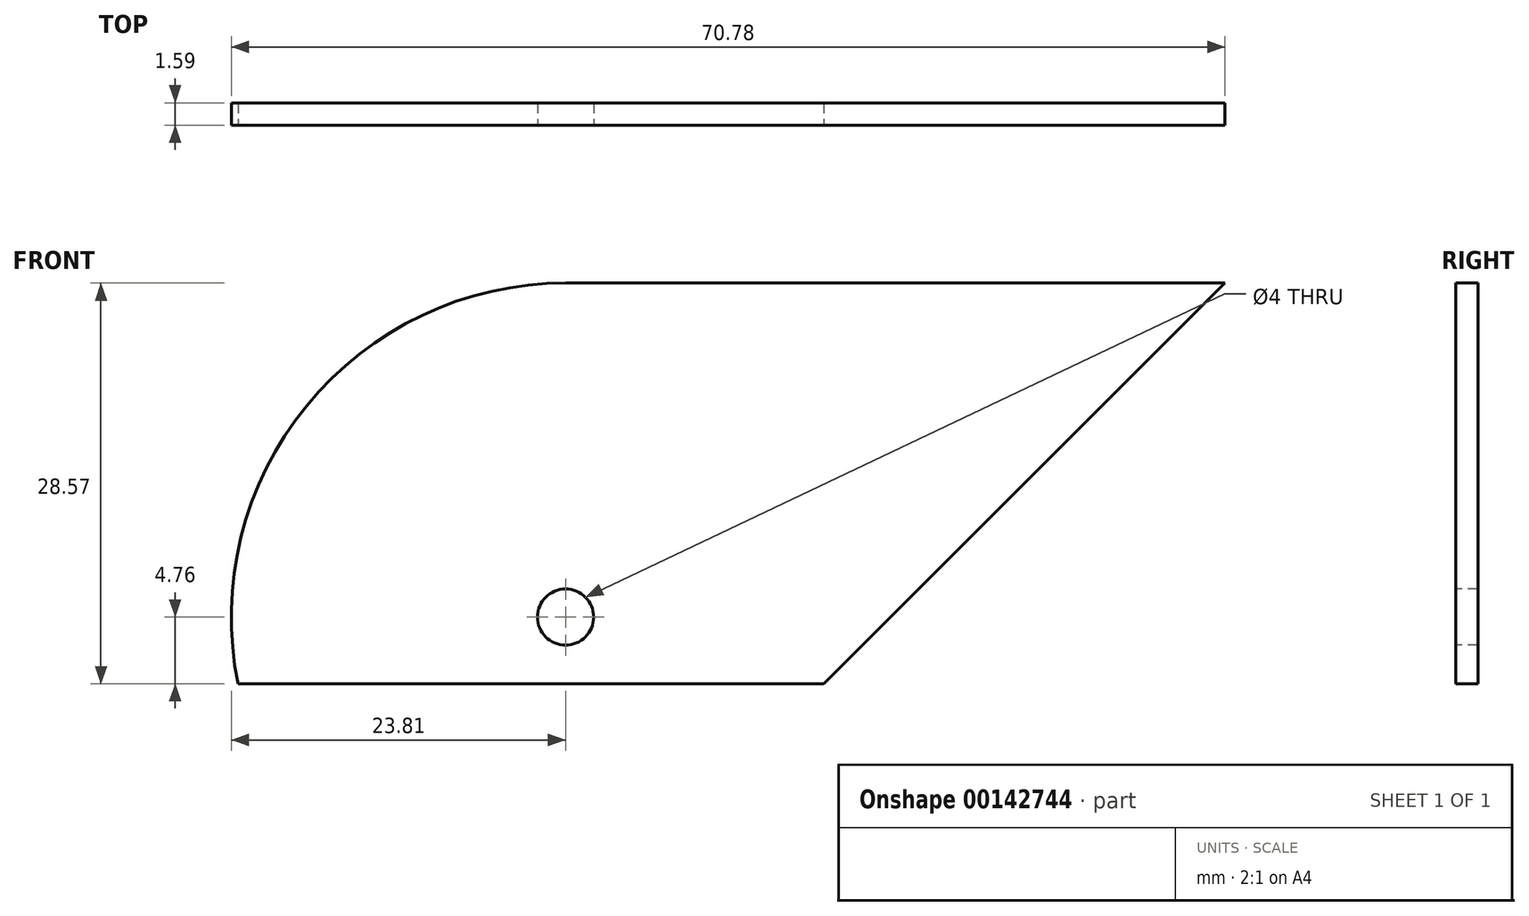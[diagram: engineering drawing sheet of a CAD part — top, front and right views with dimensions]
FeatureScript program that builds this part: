
annotation { "Feature Type Name" : "Feature", "Feature Type Description" : "" }
export const myFeature = defineFeature(function(context is Context, id is Id, definition is map)
    precondition{}
    {
        {
            var Q0;
            Q0=qCreatedBy(makeId("Front.planeOp"),FACE);
            var sketch = newSketch(context, id + "F0", { "sketchPlane" : qUnion([Q0])});
            skPoint(sketch, "E0", {"position": v(0, 0) * mm});
            skPoint(sketch, "E1", {"position": v(-111.76, 0) * mm});
            skCircle(sketch, "E2", {"center": v(-111.76, 0) * mm, "radius": 15.08 * mm});
            skLineSegment(sketch, "E3", {"start": v(-136.35, -6.35) * mm, "end": v(-92.71, -6.35) * mm});
            skLineSegment(sketch, "E4", {"start": v(-92.71, -6.35) * mm, "end": v(-60.96, 25.4) * mm});
            skLineSegment(sketch, "E5", {"start": v(-60.96, 25.4) * mm, "end": v(-111.76, 25.4) * mm});
            skArc(sketch, "E6", {"start": v(-111.76, 25.4) * mm, "mid": v(-131.84, 15.55) * mm, "end": v(-136.35, -6.35) * mm});
            skArc(sketch, "E7.0", {"start": v(-111.76, 23.81) * mm, "mid": v(-130.2, 15.06) * mm, "end": v(-135.1, -4.76) * mm});
            skLineSegment(sketch, "E7.1", {"start": v(-64.8, 23.81) * mm, "end": v(-111.76, 23.81) * mm});
            skLineSegment(sketch, "E7.2", {"start": v(-93.37, -4.76) * mm, "end": v(-64.8, 23.81) * mm});
            skLineSegment(sketch, "E7.3", {"start": v(-135.1, -4.76) * mm, "end": v(-93.37, -4.76) * mm});
            skSolve(sketch);
        }
        {
            var Q0;
            Q0=qCreatedBy(makeId("Front.planeOp"),FACE);
            cPlane(context, id + "F1", {"entities" : qUnion([Q0]), "cplaneType" : CPlaneType.OFFSET, "offset" : 22.22 * mm, "width" : 152.4 * mm, "height" : 152.4 * mm});
        }
        {
            var Q0;
            Q0=qCreatedBy(id+"F1.planeOp",FACE);
            var sketch = newSketch(context, id + "F2", { "sketchPlane" : qUnion([Q0])});
            skPoint(sketch, "E8", {"position": v(-111.76, 0) * mm});
            skArc(sketch, "E9.0", {"start": v(-111.76, 23.81) * mm, "mid": v(-130.2, 15.06) * mm, "end": v(-135.1, -4.76) * mm});
            skLineSegment(sketch, "E9.1", {"start": v(-135.1, -4.76) * mm, "end": v(-93.37, -4.76) * mm});
            skLineSegment(sketch, "E9.2", {"start": v(-93.37, -4.76) * mm, "end": v(-64.8, 23.81) * mm});
            skLineSegment(sketch, "E9.3", {"start": v(-64.8, 23.81) * mm, "end": v(-111.76, 23.81) * mm});
            skCircle(sketch, "E10", {"center": v(-111.76, 0) * mm, "radius": 2 * mm});
            skSolve(sketch);
        }
        {
            var Q0;
            Q0 = qSketchRegion(id + "F2", true);
            extrude(context, id + "F3", {"entities" : qUnion([Q0]), "oppositeDirection" : true, "depth" : 1.59 * mm});
        }
    });
